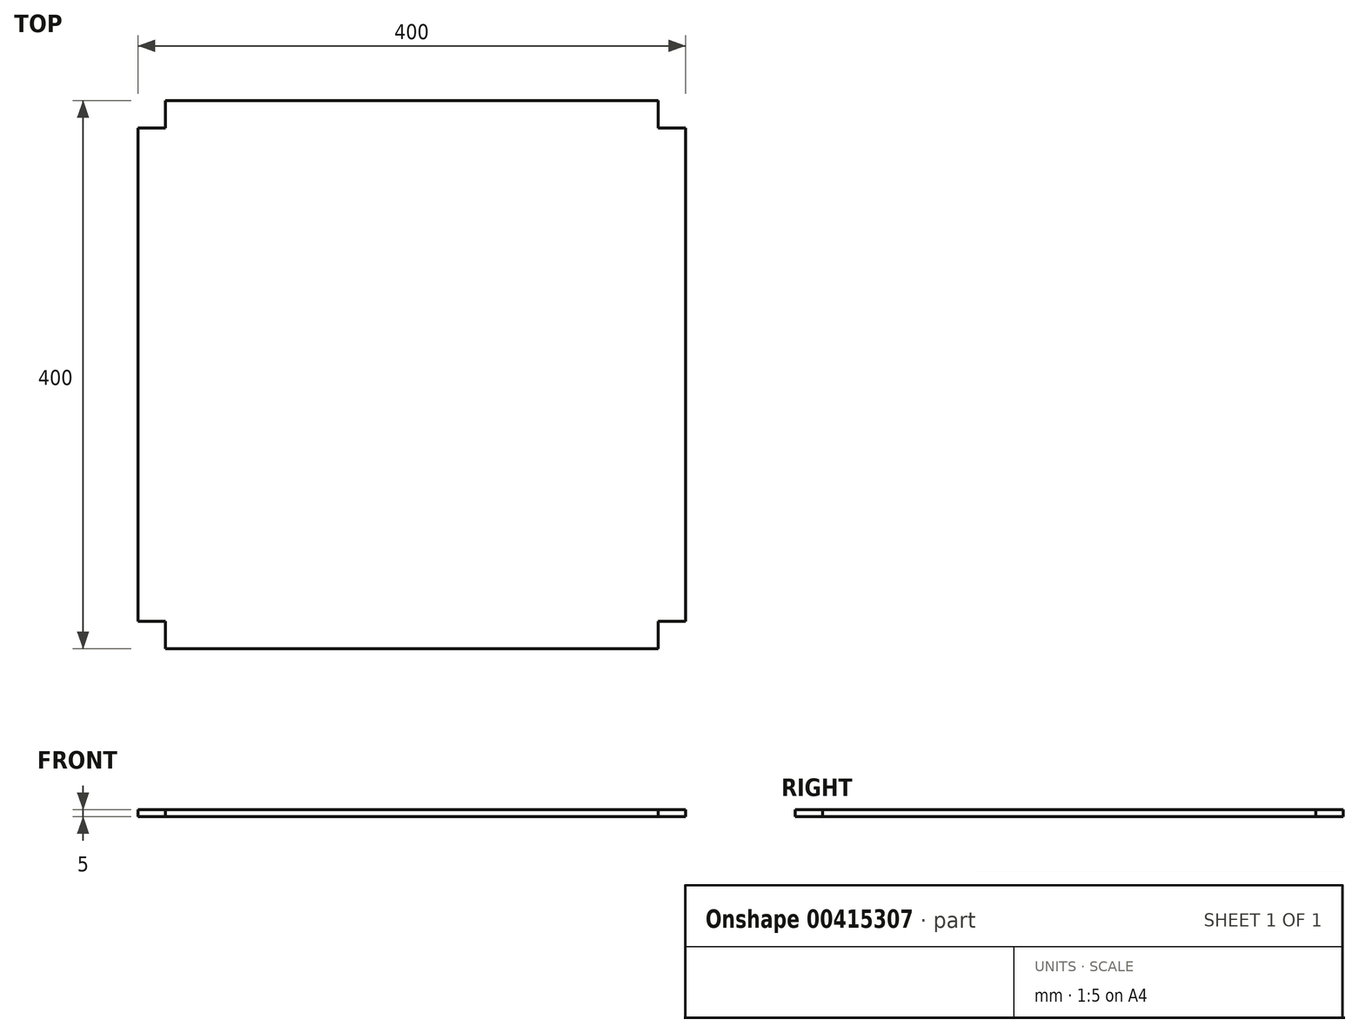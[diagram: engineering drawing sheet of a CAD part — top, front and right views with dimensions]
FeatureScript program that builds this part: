
annotation { "Feature Type Name" : "Feature", "Feature Type Description" : "" }
export const myFeature = defineFeature(function(context is Context, id is Id, definition is map)
    precondition{}
    {
        {
            var Q0;
            Q0=qCreatedBy(makeId("Top.planeOp"),FACE);
            var sketch = newSketch(context, id + "F0", { "sketchPlane" : qUnion([Q0])});
            skLineSegment(sketch, "E0.bottom", {"start": v(-319, 343.42) * mm, "end": v(41, 343.42) * mm});
            skLineSegment(sketch, "E0.top", {"start": v(-319, -56.58) * mm, "end": v(41, -56.58) * mm});
            skLineSegment(sketch, "E0.left", {"start": v(-339, 323.42) * mm, "end": v(-339, -36.58) * mm});
            skLineSegment(sketch, "E0.right", {"start": v(61, 323.42) * mm, "end": v(61, -36.58) * mm});
            skLineSegment(sketch, "E1.top", {"start": v(-339, 323.42) * mm, "end": v(-319, 323.42) * mm});
            skLineSegment(sketch, "E1.right", {"start": v(-319, 343.42) * mm, "end": v(-319, 323.42) * mm});
            skLineSegment(sketch, "E2.top", {"start": v(61, 323.42) * mm, "end": v(41, 323.42) * mm});
            skLineSegment(sketch, "E2.right", {"start": v(41, 343.42) * mm, "end": v(41, 323.42) * mm});
            skLineSegment(sketch, "E3.top", {"start": v(61, -36.58) * mm, "end": v(41, -36.58) * mm});
            skLineSegment(sketch, "E3.right", {"start": v(41, -56.58) * mm, "end": v(41, -36.58) * mm});
            skLineSegment(sketch, "E4.top", {"start": v(-339, -36.58) * mm, "end": v(-319, -36.58) * mm});
            skLineSegment(sketch, "E4.right", {"start": v(-319, -56.58) * mm, "end": v(-319, -36.58) * mm});
            skSolve(sketch);
        }
        {
            var Q0;
            Q0=makeQuery(id+"F0.imprint","IMPRINT",FACE,{"disambiguationData":[TD([[makeQuery(id+"F0.imprint","IMPRINT",EDGE,{"derivedFrom":sQuery(id+"F0.wireOp",EDGE,"E0.bottom")}),-1.0]])]});
            extrude(context, id + "F1", {"entities" : qUnion([Q0]), "depth" : 5 * mm});
        }
    });
